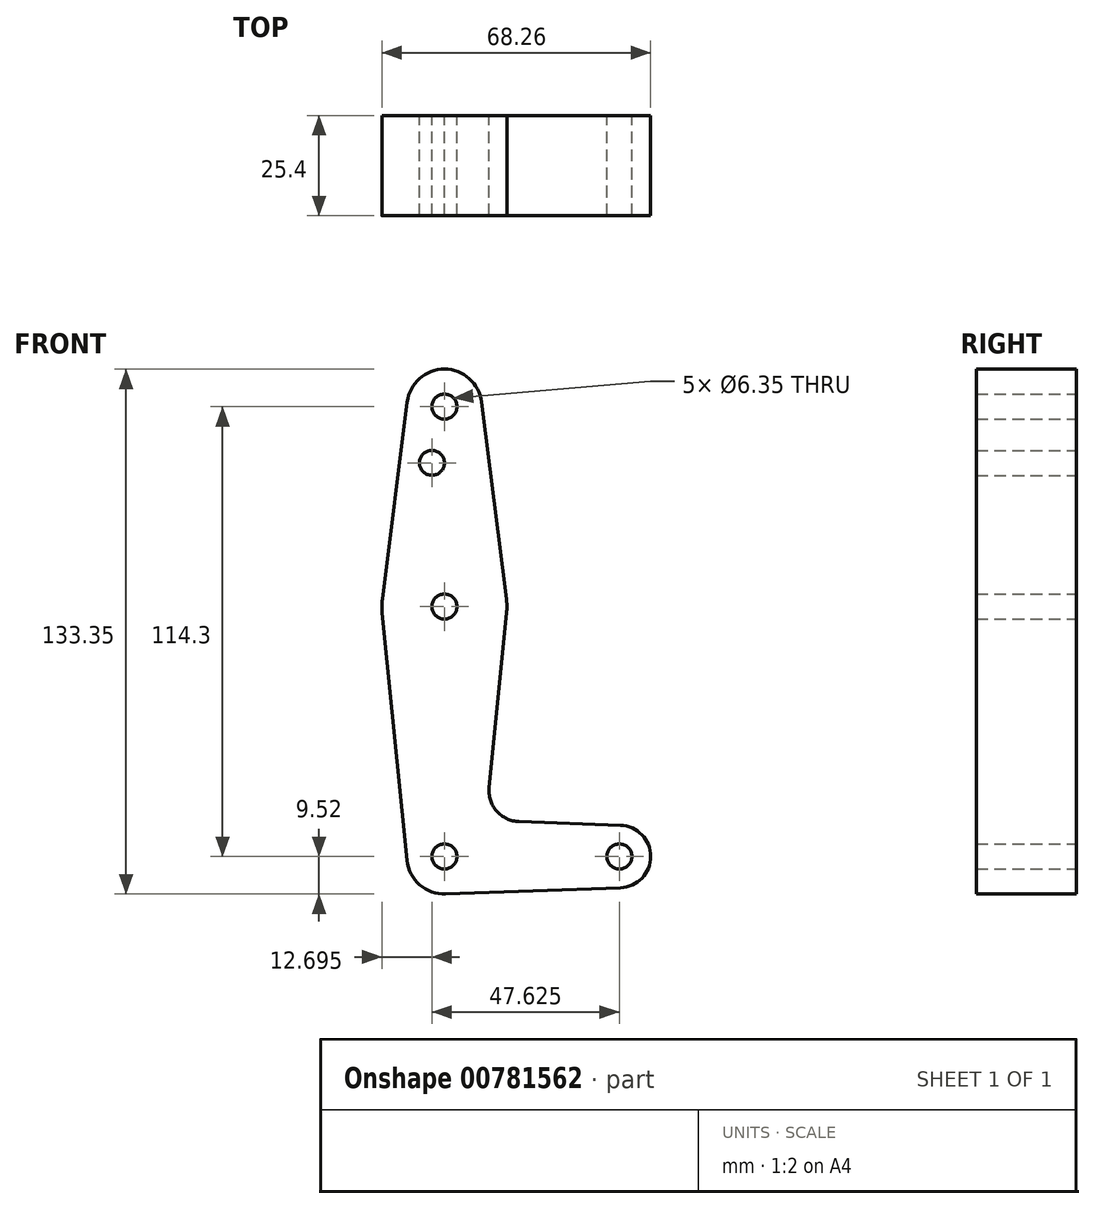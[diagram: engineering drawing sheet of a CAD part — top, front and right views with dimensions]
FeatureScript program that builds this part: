
annotation { "Feature Type Name" : "Feature", "Feature Type Description" : "" }
export const myFeature = defineFeature(function(context is Context, id is Id, definition is map)
    precondition{}
    {
        {
            var Q0;
            Q0=qCreatedBy(makeId("Front.planeOp"),FACE);
            var sketch = newSketch(context, id + "F0", { "sketchPlane" : qUnion([Q0])});
            skLineSegment(sketch, "E0", {"start": v(0, 0) * mm, "end": v(0, 114.3) * mm, "construction": true});
            skLineSegment(sketch, "E1", {"start": v(0, 0) * mm, "end": v(44.45, 0) * mm, "construction": true});
            skCircle(sketch, "E2", {"center": v(0, 114.3) * mm, "radius": 9.53 * mm});
            skCircle(sketch, "E3", {"center": v(0, 63.5) * mm, "radius": 15.88 * mm});
            skCircle(sketch, "E4", {"center": v(0, 0) * mm, "radius": 9.53 * mm});
            skCircle(sketch, "E5", {"center": v(44.45, 0) * mm, "radius": 7.94 * mm});
            skLineSegment(sketch, "E6", {"start": v(-9.45, 115.5) * mm, "end": v(-15.75, 65.48) * mm});
            skCircle(sketch, "E7", {"center": v(0, 114.3) * mm, "radius": 3.18 * mm});
            skCircle(sketch, "E8", {"center": v(-3.18, 100.03) * mm, "radius": 3.18 * mm});
            skCircle(sketch, "E9", {"center": v(0, 63.5) * mm, "radius": 3.18 * mm});
            skCircle(sketch, "E10", {"center": v(0, 0) * mm, "radius": 3.18 * mm});
            skCircle(sketch, "E11", {"center": v(44.45, 0) * mm, "radius": 3.18 * mm});
            skLineSegment(sketch, "E12", {"start": v(15.8, 61.91) * mm, "end": v(11.34, 17.6) * mm});
            skLineSegment(sketch, "E13", {"start": v(18.97, 8.85) * mm, "end": v(44.73, 7.93) * mm});
            skLineSegment(sketch, "E14", {"start": v(-15.8, 61.91) * mm, "end": v(-9.48, -0.95) * mm});
            skArc(sketch, "E15.filletArc", {"start": v(11.34, 17.6) * mm, "mid": v(13.26, 11.57) * mm, "end": v(18.97, 8.85) * mm});
            skLineSegment(sketch, "E16", {"start": v(9.45, 115.5) * mm, "end": v(15.75, 65.48) * mm});
            skLineSegment(sketch, "E17", {"start": v(0.34, -9.52) * mm, "end": v(44.73, -7.93) * mm});
            skSolve(sketch);
        }
        {
            var Q0;
            Q0 = qSketchRegion(id + "F0", true);
            extrude(context, id + "F1", {"entities" : qUnion([Q0]), "depth" : 25.4 * mm, "offsetDistance" : 25.4 * mm});
        }
    });
